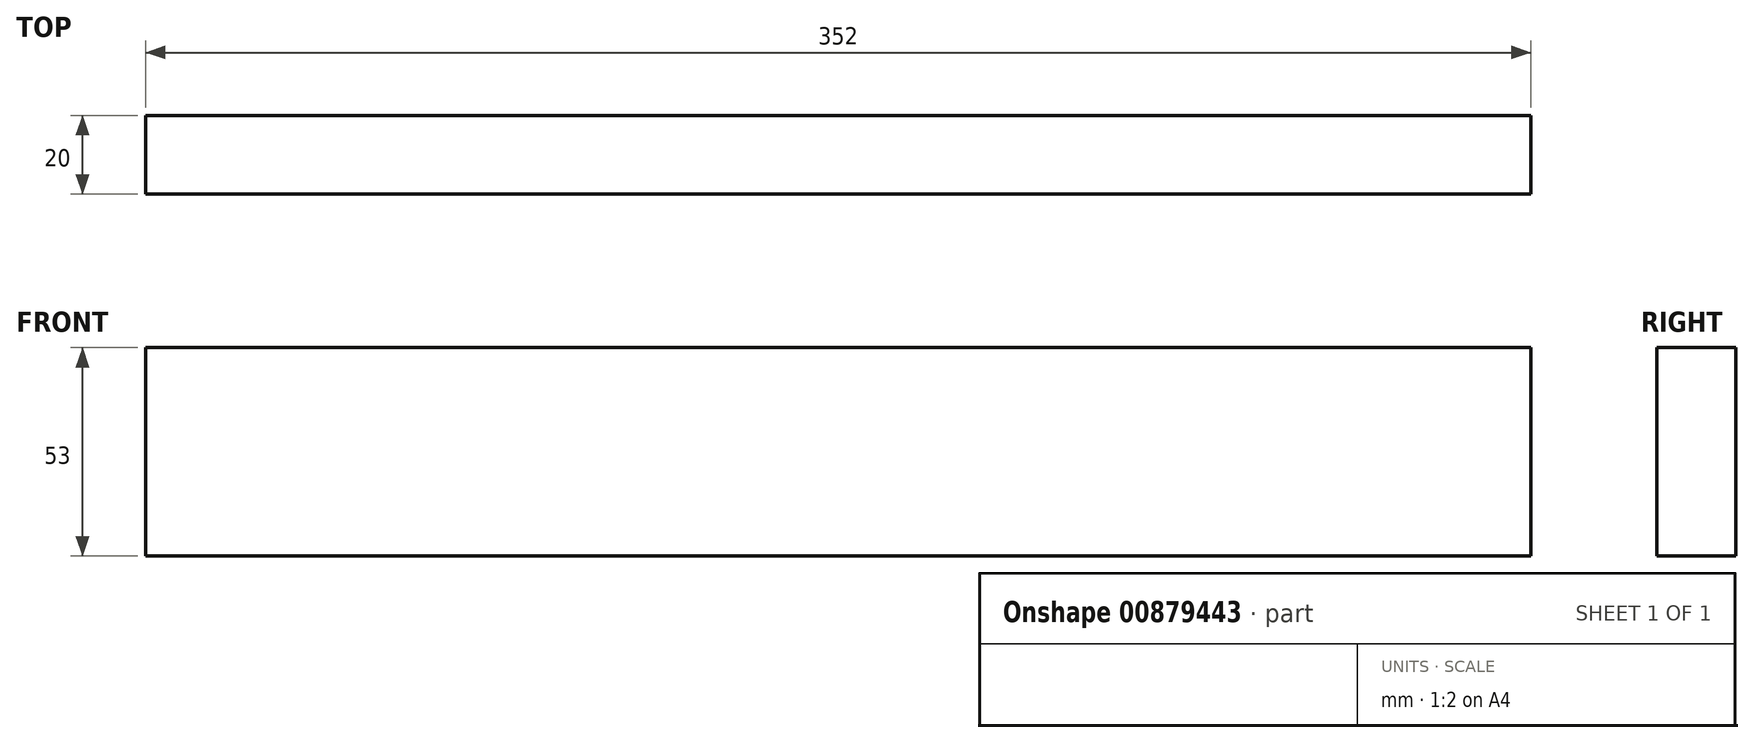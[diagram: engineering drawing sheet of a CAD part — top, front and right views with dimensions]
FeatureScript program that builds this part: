
annotation { "Feature Type Name" : "Feature", "Feature Type Description" : "" }
export const myFeature = defineFeature(function(context is Context, id is Id, definition is map)
    precondition{}
    {
        {
            var Q0;
            Q0=qCreatedBy(makeId("Front.planeOp"),FACE);
            var sketch = newSketch(context, id + "F0", { "sketchPlane" : qUnion([Q0])});
            skLineSegment(sketch, "E0.bottom", {"start": v(-176, 26.5) * mm, "end": v(176, 26.5) * mm});
            skLineSegment(sketch, "E0.top", {"start": v(-176, -26.5) * mm, "end": v(176, -26.5) * mm});
            skLineSegment(sketch, "E0.left", {"start": v(-176, 26.5) * mm, "end": v(-176, -26.5) * mm});
            skLineSegment(sketch, "E0.right", {"start": v(176, 26.5) * mm, "end": v(176, -26.5) * mm});
            skPoint(sketch, "E0.middle", {"position": v(0, 0) * mm});
            skSolve(sketch);
        }
        {
            var Q0;
            Q0=qSketchRegion(id+"F0",true);
            extrude(context, id + "F1", {"entities" : qUnion([Q0]), "flatOperationType" : FlatOperationType.REMOVE, "depth" : 20 * mm, "offsetDistance" : 25 * mm, "domain" : OperationDomain.MODEL, "symmetric" : true});
        }
    });
